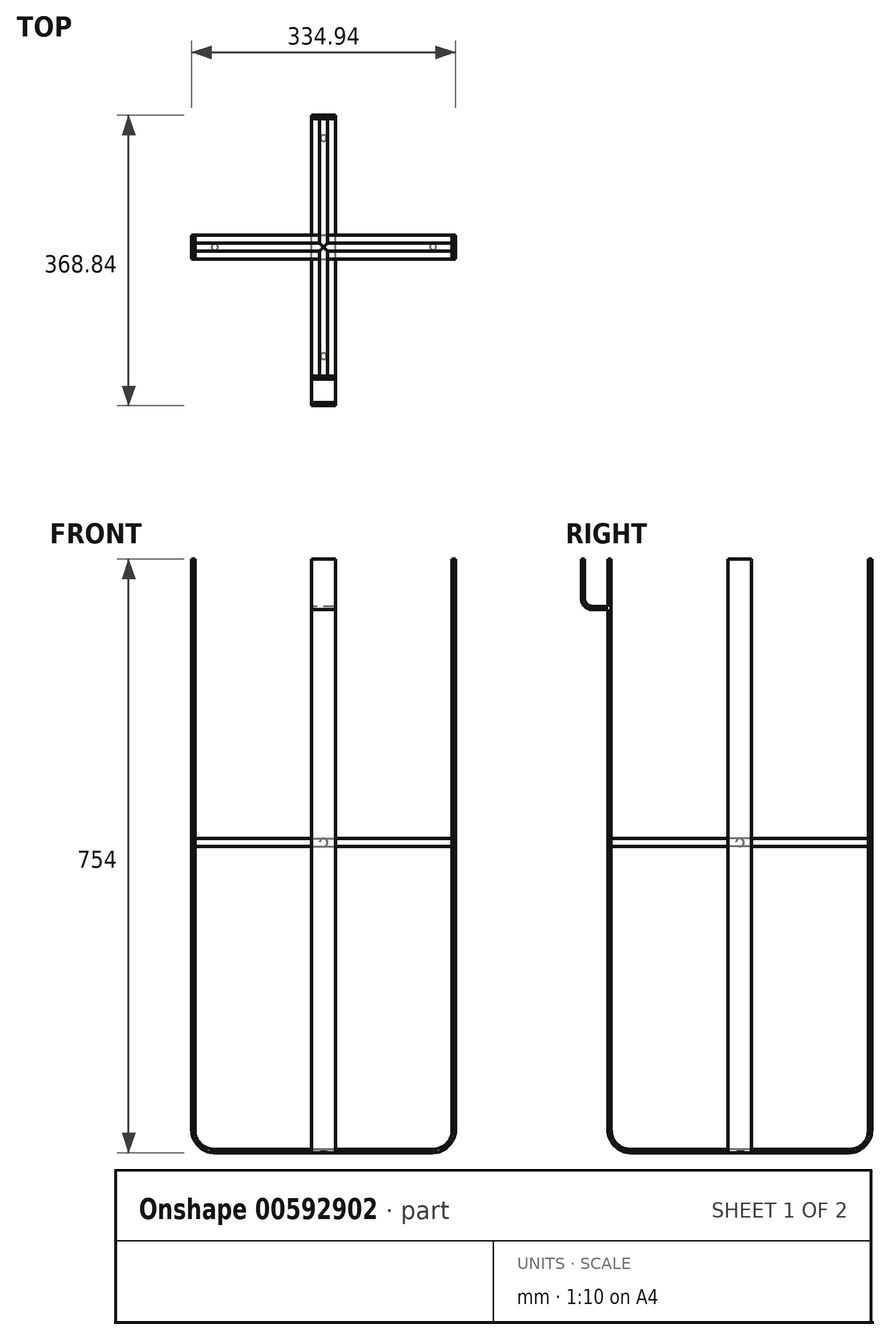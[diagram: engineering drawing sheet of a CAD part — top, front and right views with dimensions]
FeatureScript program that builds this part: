
annotation { "Feature Type Name" : "Feature", "Feature Type Description" : "" }
export const myFeature = defineFeature(function(context is Context, id is Id, definition is map)
    precondition{}
    {
        {
            var Q0;
            Q0=qCreatedBy(makeId("Right.planeOp"),FACE);
            var sketch = newSketch(context, id + "F0", { "sketchPlane" : qUnion([Q0])});
            skLineSegment(sketch, "E0", {"start": v(0, 0) * mm, "end": v(0, -725) * mm});
            skLineSegment(sketch, "E1", {"start": v(25, -750) * mm, "end": v(302, -750) * mm});
            skLineSegment(sketch, "E2", {"start": v(327, -725) * mm, "end": v(327, 0) * mm});
            skPoint(sketch, "E3.visualSharp", {"position": v(0, -750) * mm});
            skArc(sketch, "E3.filletArc", {"start": v(0, -725) * mm, "mid": v(7.32, -742.68) * mm, "end": v(25, -750) * mm});
            skPoint(sketch, "E4.visualSharp", {"position": v(327, -750) * mm});
            skArc(sketch, "E4.filletArc", {"start": v(302, -750) * mm, "mid": v(319.68, -742.68) * mm, "end": v(327, -725) * mm});
            skLineSegment(sketch, "E5.0", {"start": v(331, -725) * mm, "end": v(331, 0) * mm});
            skLineSegment(sketch, "E5.1", {"start": v(-4, 0) * mm, "end": v(-4, -725) * mm});
            skArc(sketch, "E5.2", {"start": v(-4, -725) * mm, "mid": v(4.5, -745.5) * mm, "end": v(25, -754) * mm});
            skLineSegment(sketch, "E5.3", {"start": v(25, -754) * mm, "end": v(302, -754) * mm});
            skArc(sketch, "E5.4", {"start": v(302, -754) * mm, "mid": v(322.5, -745.5) * mm, "end": v(331, -725) * mm});
            skLineSegment(sketch, "E6", {"start": v(-4, 0) * mm, "end": v(0, 0) * mm});
            skLineSegment(sketch, "E7", {"start": v(327, 0) * mm, "end": v(331, 0) * mm});
            skSolve(sketch);
        }
        {
            var Q0;
            Q0=makeQuery(id+"F0.imprint","IMPRINT",FACE,{"disambiguationData":[TD([[makeQuery(id+"F0.imprint","IMPRINT",EDGE,{"derivedFrom":sQuery(id+"F0.wireOp",EDGE,"E0")}),-1.0]])]});
            extrude(context, id + "F1", {"entities" : qUnion([Q0]), "depth" : 30 * mm, "offsetDistance" : 25 * mm});
        }
        {
            var Q0;
            Q0=qCreatedBy(makeId("Front.planeOp"),FACE);
            cPlane(context, id + "F2", {"entities" : qUnion([Q0]), "cplaneType" : CPlaneType.OFFSET, "offset" : 148.5 * mm, "oppositeDirection" : true, "width" : 150 * mm, "height" : 150 * mm});
        }
        {
            var Q0;
            Q0=qCreatedBy(makeId("Right.planeOp"),FACE);
            cPlane(context, id + "F3", {"entities" : qUnion([Q0]), "cplaneType" : CPlaneType.OFFSET, "offset" : 15 * mm, "width" : 150 * mm, "height" : 150 * mm});
        }
        {
            var Q0;
            Q0=qCreatedBy(id+"F3.planeOp",FACE);
            var sketch = newSketch(context, id + "F4", { "sketchPlane" : qUnion([Q0])});
            skLineSegment(sketch, "E8.bottom", {"start": v(178.5, -753.97) * mm, "end": v(148.5, -753.97) * mm});
            skLineSegment(sketch, "E8.top", {"start": v(178.5, -749.97) * mm, "end": v(148.5, -749.97) * mm});
            skLineSegment(sketch, "E8.left", {"start": v(178.5, -753.97) * mm, "end": v(178.5, -749.97) * mm});
            skLineSegment(sketch, "E8.right", {"start": v(148.5, -753.97) * mm, "end": v(148.5, -749.97) * mm});
            skSolve(sketch);
        }
        {
            var Q0;
            Q0=qCreatedBy(id+"F2.planeOp",FACE);
            var sketch = newSketch(context, id + "F5", { "sketchPlane" : qUnion([Q0])});
            skLineSegment(sketch, "E9", {"start": v(-148.5, 0) * mm, "end": v(-148.5, -725) * mm});
            skLineSegment(sketch, "E10", {"start": v(-123.5, -750) * mm, "end": v(153.5, -750) * mm});
            skLineSegment(sketch, "E11", {"start": v(178.5, -725) * mm, "end": v(178.5, 0) * mm});
            skPoint(sketch, "E12.visualSharp", {"position": v(-148.5, -750) * mm});
            skArc(sketch, "E12.filletArc", {"start": v(-148.5, -725) * mm, "mid": v(-141.18, -742.68) * mm, "end": v(-123.5, -750) * mm});
            skPoint(sketch, "E13.visualSharp", {"position": v(178.5, -750) * mm});
            skArc(sketch, "E13.filletArc", {"start": v(153.5, -750) * mm, "mid": v(171.18, -742.68) * mm, "end": v(178.5, -725) * mm});
            skSolve(sketch);
        }
        {
            var Q0;
            Q0 = qSketchRegion(id + "F4", true);
            var Q1;
            Q1 = qConstructionFilter(qBodyType(qCreatedBy(id + "F5" ,EDGE), BodyType.WIRE), ConstructionObject.NO);
            sweep(context, id + "F6", {"operationType" : NewBodyOperationType.ADD, "profiles" : qUnion([Q0]), "path" : qUnion([Q1])});
        }
        {
            var Q0;
            Q0=makeQuery(id+"F6.opSweep","SWEPT_FACE",FACE,{"disambiguationData":[OSD([sQuery(id+"F4.wireOp",EDGE,"E8.bottom"),sQuery(id+"F5.wireOp",EDGE,"E11")])]});
            var sketch = newSketch(context, id + "F7", { "sketchPlane" : qUnion([Q0])});
            skCircle(sketch, "E14", {"center": v(163.5, -360) * mm, "radius": 5 * mm});
            skSolve(sketch);
        }
        {
            var Q0;
            Q0=makeQuery(id+"F7.imprint","IMPRINT",FACE,{"disambiguationData":[TD([[makeQuery(id+"F7.imprint","IMPRINT",EDGE,{"derivedFrom":sQuery(id+"F7.wireOp",EDGE,"E14")}),1.0]])]});
            extrude(context, id + "F8", {"entities" : qUnion([Q0]), "operationType" : NewBodyOperationType.ADD, "oppositeDirection" : true, "depth" : 334 * mm, "offsetDistance" : 25 * mm});
        }
        {
            var Q0;
            Q0=makeQuery(id+"F1.opExtrude","SWEPT_FACE",FACE,{"disambiguationData":[OSD([sQuery(id+"F0.wireOp",EDGE,"E5.1")])]});
            var sketch = newSketch(context, id + "F9", { "sketchPlane" : qUnion([Q0])});
            skCircle(sketch, "E15", {"center": v(15, -360) * mm, "radius": 5 * mm});
            skSolve(sketch);
        }
        {
            var Q0;
            Q0 = qSketchRegion(id + "F9", true);
            extrude(context, id + "F10", {"entities" : qUnion([Q0]), "operationType" : NewBodyOperationType.ADD, "oppositeDirection" : true, "depth" : 334 * mm, "offsetDistance" : 25 * mm});
        }
        {
            var Q0;
            Q0=makeQuery(id+"F1.opExtrude","SWEPT_FACE",FACE,{"disambiguationData":[OSD([sQuery(id+"F0.wireOp",EDGE,"E5.3")])]});
            var sketch = newSketch(context, id + "F11", { "sketchPlane" : qUnion([Q0])});
            skCircle(sketch, "E16", {"center": v(15, -25) * mm, "radius": 4 * mm});
            skCircle(sketch, "E17", {"center": v(15, -302) * mm, "radius": 4 * mm});
            skCircle(sketch, "E18", {"center": v(-123.1, -163.74) * mm, "radius": 4 * mm});
            skCircle(sketch, "E19", {"center": v(154.12, -164.25) * mm, "radius": 4 * mm});
            skSolve(sketch);
        }
        {
            var Q0;
            Q0 = qSketchRegion(id + "F11", true);
            extrude(context, id + "F12", {"entities" : qUnion([Q0]), "operationType" : NewBodyOperationType.REMOVE, "oppositeDirection" : true, "depth" : 25 * mm, "offsetDistance" : 25 * mm});
        }
        {
            var Q0;
            Q0=qCreatedBy(id+"F3.planeOp",FACE);
            var sketch = newSketch(context, id + "F13", { "sketchPlane" : qUnion([Q0])});
            skLineSegment(sketch, "E20", {"start": v(-3.84, -60) * mm, "end": v(-23.84, -60) * mm});
            skLineSegment(sketch, "E21", {"start": v(-33.84, -50) * mm, "end": v(-33.84, 0) * mm});
            skPoint(sketch, "E22.visualSharp", {"position": v(-33.84, -60) * mm});
            skArc(sketch, "E22.filletArc", {"start": v(-33.84, -50) * mm, "mid": v(-30.91, -57.07) * mm, "end": v(-23.84, -60) * mm});
            skLineSegment(sketch, "E23.0", {"start": v(-37.84, -50) * mm, "end": v(-37.84, 0) * mm});
            skArc(sketch, "E23.1", {"start": v(-37.84, -50) * mm, "mid": v(-33.74, -59.9) * mm, "end": v(-23.84, -64) * mm});
            skLineSegment(sketch, "E23.2", {"start": v(-3.84, -64) * mm, "end": v(-23.84, -64) * mm});
            skLineSegment(sketch, "E24", {"start": v(-37.84, 0) * mm, "end": v(-33.84, 0) * mm});
            skLineSegment(sketch, "E25", {"start": v(-3.84, -60) * mm, "end": v(-3.84, -64) * mm});
            skSolve(sketch);
        }
        {
            var Q0;
            Q0 = qSketchRegion(id + "F13", true);
            extrude(context, id + "F14", {"entities" : qUnion([Q0]), "operationType" : NewBodyOperationType.ADD, "depth" : 15 * mm, "offsetDistance" : 25 * mm, "hasSecondDirection" : true, "secondDirectionOppositeDirection" : true, "secondDirectionDepth" : 15 * mm});
        }
    });
